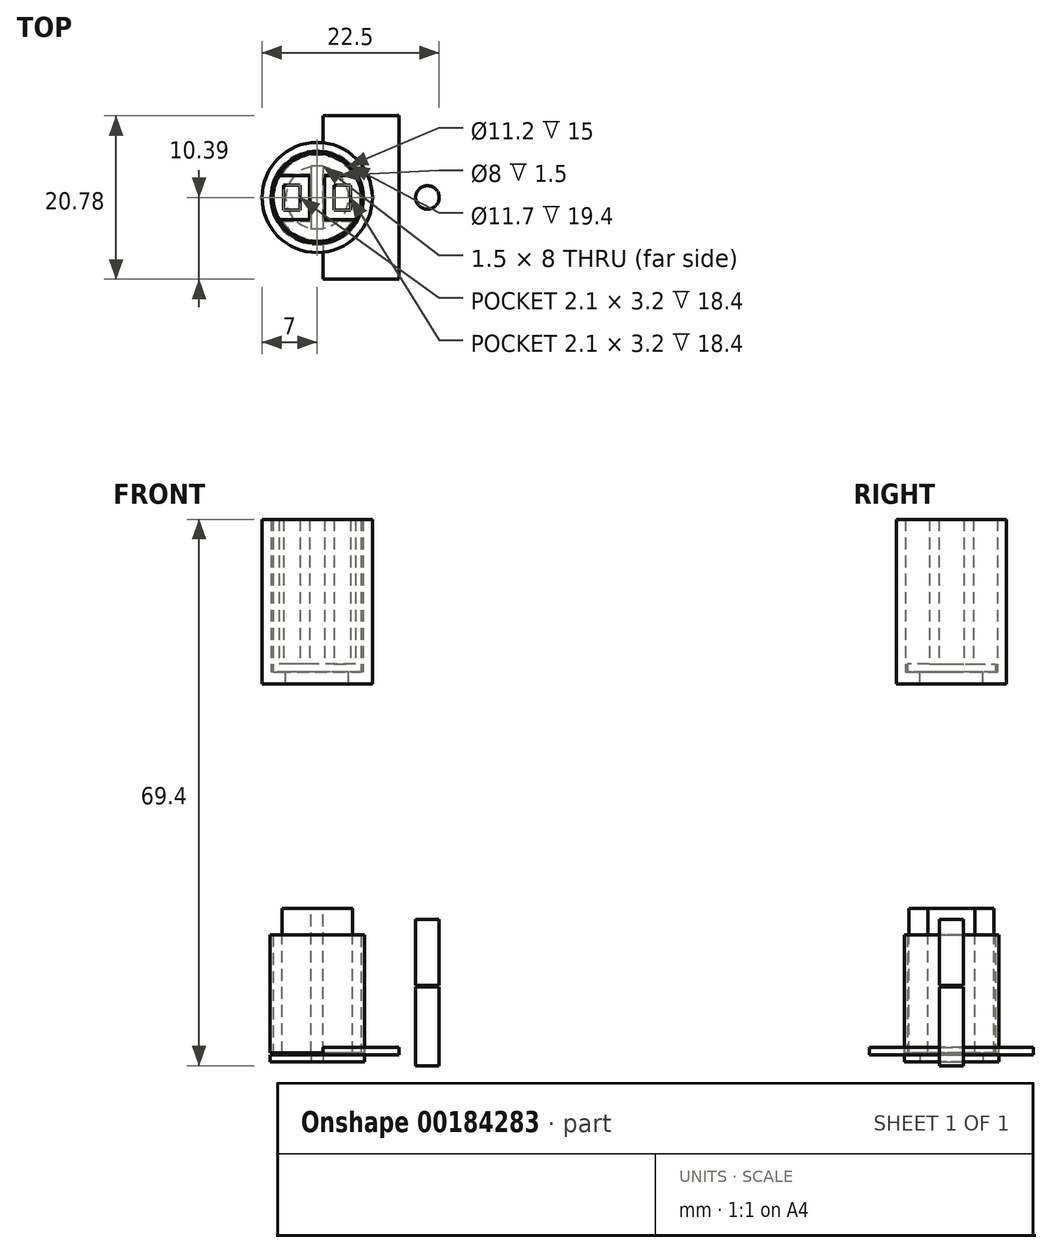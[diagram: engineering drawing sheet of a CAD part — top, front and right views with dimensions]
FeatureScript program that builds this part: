
annotation { "Feature Type Name" : "Feature", "Feature Type Description" : "" }
export const myFeature = defineFeature(function(context is Context, id is Id, definition is map)
    precondition{}
    {
        {
            assignVariable(context, id + "F0", {"name" : "dMaskThick", "anyValue" : .9});
        }
        {
            assignVariable(context, id + "F1", {"name" : "outerRingHeight", "anyValue" : 10});
        }
        {
            assignVariable(context, id + "F2", {"name" : "bottomLip", "anyValue" : .5});
        }
        {
            assignVariable(context, id + "F3", {"name" : "innerSquareHeight", "anyValue" : getVariable(context, 'outerRingHeight') - getVariable(context, 'dMaskThick') - getVariable(context, 'bottomLip')});
        }
        {
            assignVariable(context, id + "F4", {"name" : "innerRingHeight", "anyValue" : 15});
        }
        {
            var Q0;
            Q0=qCreatedBy(makeId("Top.planeOp"),FACE);
            var sketch = newSketch(context, id + "F5", { "sketchPlane" : qUnion([Q0])});
            skCircle(sketch, "E0", {"center": v(0, 0) * mm, "radius": 6 * mm});
            skCircle(sketch, "E1", {"center": v(0, 0) * mm, "radius": 17 * mm});
            skCircle(sketch, "E2", {"center": v(0, 0) * mm, "radius": 8.1 * mm});
            skCircle(sketch, "E3.cCircle", {"center": v(0, 0) * mm, "radius": 15 * mm});
            skLineSegment(sketch, "E3.0", {"start": v(10.6, -10.6) * mm, "end": v(-10.6, -10.6) * mm});
            skLineSegment(sketch, "E3.1", {"start": v(-10.6, -10.6) * mm, "end": v(-10.6, 10.6) * mm});
            skLineSegment(sketch, "E3.2", {"start": v(-10.6, 10.6) * mm, "end": v(10.6, 10.6) * mm});
            skLineSegment(sketch, "E3.3", {"start": v(10.6, 10.6) * mm, "end": v(10.6, -10.6) * mm});
            skLineSegment(sketch, "E4", {"start": v(-25.02, 0) * mm, "end": v(35.29, 0) * mm, "construction": true});
            skLineSegment(sketch, "E5", {"start": v(0, 24.03) * mm, "end": v(0, -20.76) * mm, "construction": true});
            skSolve(sketch);
        }
        {
            var Q0;
            Q0=makeQuery(id+"F5.imprint","IMPRINT",FACE,{"disambiguationData":[TD([[makeQuery(id+"F5.imprint","IMPRINT",EDGE,{"derivedFrom":sQuery(id+"F5.wireOp",EDGE,"E1")}),1.0]])]});
            var Q1;
            {var subQ0=sQuery(id+"F5.wireOp",EDGE,"E3.2");Q1=makeQuery(id+"F5.imprint","IMPRINT",FACE,{"disambiguationData":[TD([[makeQuery(id+"F5.imprint","IMPRINT",EDGE,{"derivedFrom":subQ0}),1.0]])]});}
            var Q2;
            {var subQ0=sQuery(id+"F5.wireOp",EDGE,"E3.1");Q2=makeQuery(id+"F5.imprint","IMPRINT",FACE,{"disambiguationData":[TD([[makeQuery(id+"F5.imprint","IMPRINT",EDGE,{"derivedFrom":subQ0}),1.0]])]});}
            var Q3;
            {var subQ0=sQuery(id+"F5.wireOp",EDGE,"E3.3");Q3=makeQuery(id+"F5.imprint","IMPRINT",FACE,{"disambiguationData":[TD([[makeQuery(id+"F5.imprint","IMPRINT",EDGE,{"derivedFrom":subQ0}),1.0]])]});}
            var Q4;
            {var subQ0=sQuery(id+"F5.wireOp",EDGE,"E3.0");Q4=makeQuery(id+"F5.imprint","IMPRINT",FACE,{"disambiguationData":[TD([[makeQuery(id+"F5.imprint","IMPRINT",EDGE,{"derivedFrom":subQ0}),1.0]])]});}
            var Q5;
            Q5=makeQuery(id+"F5.imprint","IMPRINT",FACE,{"disambiguationData":[TD([[makeQuery(id+"F5.imprint","IMPRINT",EDGE,{"derivedFrom":sQuery(id+"F5.wireOp",EDGE,"E2")}),-1.0]])]});
            var Q6;
            Q6=makeQuery(id+"F5.imprint","IMPRINT",FACE,{"disambiguationData":[TD([[makeQuery(id+"F5.imprint","IMPRINT",EDGE,{"derivedFrom":sQuery(id+"F5.wireOp",EDGE,"E0")}),-1.0]])]});
            extrude(context, id + "F6", {"entities" : qUnion([Q0, Q1, Q2, Q3, Q4, Q5, Q6]), "depth" : (getVariable(context, 'bottomLip')) * mm});
        }
        {
            var Q0;
            Q0=makeQuery(id+"F5.imprint","IMPRINT",FACE,{"disambiguationData":[TD([[makeQuery(id+"F5.imprint","IMPRINT",EDGE,{"derivedFrom":sQuery(id+"F5.wireOp",EDGE,"E1")}),1.0]])]});
            var Q1;
            {var subQ0=sQuery(id+"F5.wireOp",EDGE,"E3.1");Q1=makeQuery(id+"F5.imprint","IMPRINT",FACE,{"disambiguationData":[TD([[makeQuery(id+"F5.imprint","IMPRINT",EDGE,{"derivedFrom":subQ0}),1.0]])]});}
            var Q2;
            {var subQ0=sQuery(id+"F5.wireOp",EDGE,"E3.2");Q2=makeQuery(id+"F5.imprint","IMPRINT",FACE,{"disambiguationData":[TD([[makeQuery(id+"F5.imprint","IMPRINT",EDGE,{"derivedFrom":subQ0}),1.0]])]});}
            var Q3;
            {var subQ0=sQuery(id+"F5.wireOp",EDGE,"E3.3");Q3=makeQuery(id+"F5.imprint","IMPRINT",FACE,{"disambiguationData":[TD([[makeQuery(id+"F5.imprint","IMPRINT",EDGE,{"derivedFrom":subQ0}),1.0]])]});}
            var Q4;
            {var subQ0=sQuery(id+"F5.wireOp",EDGE,"E3.0");Q4=makeQuery(id+"F5.imprint","IMPRINT",FACE,{"disambiguationData":[TD([[makeQuery(id+"F5.imprint","IMPRINT",EDGE,{"derivedFrom":subQ0}),1.0]])]});}
            extrude(context, id + "F7", {"entities" : qUnion([Q0, Q1, Q2, Q3, Q4]), "operationType" : NewBodyOperationType.ADD, "depth" : getVariable(context, 'outerRingHeight') * mm});
        }
        {
            var Q0;
            Q0=makeQuery(id+"F6.opExtrude","CAP_FACE",FACE,{"disambiguationData":[OSD([sQuery(id+"F5.wireOp",EDGE,"E0"),sQuery(id+"F5.wireOp",EDGE,"E1")])],"isStart":false});
            var sketch = newSketch(context, id + "F8", { "sketchPlane" : qUnion([Q0])});
            skCircle(sketch, "E6.cCircle", {"center": v(0, 0) * mm, "radius": 14.7 * mm, "construction": true});
            skLineSegment(sketch, "E6.0", {"start": v(10.4, 10.4) * mm, "end": v(10.4, -10.4) * mm});
            skLineSegment(sketch, "E6.1", {"start": v(10.4, -10.4) * mm, "end": v(-10.4, -10.4) * mm});
            skLineSegment(sketch, "E6.2", {"start": v(-10.4, -10.4) * mm, "end": v(-10.4, 10.4) * mm});
            skLineSegment(sketch, "E6.3", {"start": v(-10.4, 10.4) * mm, "end": v(10.4, 10.4) * mm});
            skLineSegment(sketch, "E7.bottom", {"start": v(0.75, 4) * mm, "end": v(-0.75, 4) * mm});
            skLineSegment(sketch, "E7.top", {"start": v(0.75, -4) * mm, "end": v(-0.75, -4) * mm});
            skLineSegment(sketch, "E7.left", {"start": v(0.75, 4) * mm, "end": v(0.75, -4) * mm});
            skLineSegment(sketch, "E7.right", {"start": v(-0.75, 4) * mm, "end": v(-0.75, -4) * mm});
            skSolve(sketch);
        }
        {
            var Q0;
            Q0=makeQuery(id+"F8.imprint","IMPRINT",FACE,{"disambiguationData":[TD([[makeQuery(id+"F8.imprint","IMPRINT",EDGE,{"derivedFrom":sQuery(id+"F8.wireOp",EDGE,"E7.bottom")}),-1.0]])]});
            var Q1;
            Q1=makeQuery(id+"F8.imprint","IMPRINT",FACE,{"disambiguationData":[TD([[makeQuery(id+"F8.imprint","IMPRINT",EDGE,{"derivedFrom":sQuery(id+"F8.wireOp",EDGE,"E6.0")}),-1.0]])]});
            extrude(context, id + "F9", {"entities" : qUnion([Q0, Q1]), "depth" : (getVariable(context, 'dMaskThick')) * mm});
        }
        {
            var Q0;
            Q0=makeQuery(id+"F9.opExtrude","CAP_FACE",FACE,{"disambiguationData":[OSD([sQuery(id+"F8.wireOp",EDGE,"E6.0"),sQuery(id+"F8.wireOp",EDGE,"E6.1"),sQuery(id+"F8.wireOp",EDGE,"E6.2"),sQuery(id+"F8.wireOp",EDGE,"E6.3"),sQuery(id+"F8.wireOp",EDGE,"E7.bottom"),sQuery(id+"F8.wireOp",EDGE,"E7.top"),sQuery(id+"F8.wireOp",EDGE,"E7.left"),sQuery(id+"F8.wireOp",EDGE,"E7.right")])],"isStart":false});
            var sketch = newSketch(context, id + "F10", { "sketchPlane" : qUnion([Q0])});
            skCircle(sketch, "E8.cCircle", {"center": v(0, 0) * mm, "radius": 14.4 * mm, "construction": true});
            skLineSegment(sketch, "E8.0", {"start": v(10.18, 10.18) * mm, "end": v(10.18, -10.18) * mm});
            skLineSegment(sketch, "E8.1", {"start": v(10.18, -10.18) * mm, "end": v(-10.18, -10.18) * mm});
            skLineSegment(sketch, "E8.2", {"start": v(-10.18, -10.18) * mm, "end": v(-10.18, 10.18) * mm});
            skLineSegment(sketch, "E8.3", {"start": v(-10.18, 10.18) * mm, "end": v(10.18, 10.18) * mm});
            skCircle(sketch, "E9", {"center": v(0, 0) * mm, "radius": 8.1 * mm});
            skSolve(sketch);
        }
        {
            var Q0;
            Q0=qSketchRegion(id+"F10",true);
            extrude(context, id + "F11", {"entities" : qUnion([Q0]), "depth" : (getVariable(context, 'innerSquareHeight')) * mm});
        }
        {
            var Q0;
            Q0=qCreatedBy(makeId("Front.planeOp"),FACE);
            var sketch = newSketch(context, id + "F12", { "sketchPlane" : qUnion([Q0])});
            skCircle(sketch, "E10", {"center": v(8.5, 4) * mm, "radius": 1.1 * mm});
            skLineSegment(sketch, "E11", {"start": v(0, 23.51) * mm, "end": v(0, 0) * mm, "construction": true});
            skCircle(sketch, "E12", {"center": v(8.5, 7.44) * mm, "radius": 1.1 * mm});
            skCircle(sketch, "E13", {"center": v(8.5, 7.44) * mm, "radius": 1 * mm});
            skCircle(sketch, "E14", {"center": v(8.5, 4) * mm, "radius": 1 * mm});
            skSolve(sketch);
        }
        {
            var Q0;
            Q0=makeQuery(id+"F12.imprint","IMPRINT",FACE,{"disambiguationData":[TD([[makeQuery(id+"F12.imprint","IMPRINT",EDGE,{"derivedFrom":sQuery(id+"F12.wireOp",EDGE,"E13")}),1.0]])]});
            var Q1;
            Q1=makeQuery(id+"F12.imprint","IMPRINT",FACE,{"disambiguationData":[TD([[makeQuery(id+"F12.imprint","IMPRINT",EDGE,{"derivedFrom":sQuery(id+"F12.wireOp",EDGE,"E12")}),1.0]])]});
            var Q2;
            Q2=makeQuery(id+"F12.imprint","IMPRINT",FACE,{"disambiguationData":[TD([[makeQuery(id+"F12.imprint","IMPRINT",EDGE,{"derivedFrom":sQuery(id+"F12.wireOp",EDGE,"E14")}),1.0]])]});
            var Q3;
            Q3=makeQuery(id+"F12.imprint","IMPRINT",FACE,{"disambiguationData":[TD([[makeQuery(id+"F12.imprint","IMPRINT",EDGE,{"derivedFrom":sQuery(id+"F12.wireOp",EDGE,"E10")}),1.0]])]});
            var Q4;
            Q4=sQuery(id+"F12.wireOp",EDGE,"E11");
            revolve(context, id + "F13", {"operationType" : NewBodyOperationType.REMOVE, "entities" : qUnion([Q0, Q1, Q2, Q3]), "axis" : qUnion([Q4]), "revolveType" : RevolveType.FULL, "oppositeDirection" : true});
        }
        {
            var Q0;
            Q0=qCreatedBy(makeId("Front.planeOp"),FACE);
            var sketch = newSketch(context, id + "F14", { "sketchPlane" : qUnion([Q0])});
            skLineSegment(sketch, "E15", {"start": v(0, -4.37) * mm, "end": v(0, 15.91) * mm, "construction": true});
            skLineSegment(sketch, "E16", {"start": v(-23.99, 0) * mm, "end": v(22.47, 0) * mm, "construction": true});
            skLineSegment(sketch, "E17.bottom", {"start": v(5.6, 16.6) * mm, "end": v(7.6, 16.6) * mm});
            skLineSegment(sketch, "E17.top", {"start": v(5.6, 1.6) * mm, "end": v(7.6, 1.6) * mm});
            skLineSegment(sketch, "E17.left", {"start": v(5.6, 16.6) * mm, "end": v(5.6, 1.6) * mm});
            skLineSegment(sketch, "E17.right", {"start": v(7.6, 16.6) * mm, "end": v(7.6, 1.6) * mm});
            skSolve(sketch);
        }
        {
            var Q0;
            Q0=makeQuery(id+"F14.imprint","IMPRINT",FACE,{"disambiguationData":[TD([[makeQuery(id+"F14.imprint","IMPRINT",EDGE,{"derivedFrom":sQuery(id+"F14.wireOp",EDGE,"E17.bottom")}),-1.0]])]});
            var Q1;
            Q1=sQuery(id+"F14.wireOp",EDGE,"E15");
            revolve(context, id + "F15", {"entities" : qUnion([Q0]), "axis" : qUnion([Q1]), "revolveType" : RevolveType.FULL});
        }
        {
            var Q0;
            Q0=makeQuery(id+"F12.imprint","IMPRINT",FACE,{"disambiguationData":[TD([[makeQuery(id+"F12.imprint","IMPRINT",EDGE,{"derivedFrom":sQuery(id+"F12.wireOp",EDGE,"E13")}),1.0]])]});
            var Q1;
            Q1=makeQuery(id+"F12.imprint","IMPRINT",FACE,{"disambiguationData":[TD([[makeQuery(id+"F12.imprint","IMPRINT",EDGE,{"derivedFrom":sQuery(id+"F12.wireOp",EDGE,"E14")}),1.0]])]});
            var Q2;
            Q2=sQuery(id+"F12.wireOp",EDGE,"E11");
            revolve(context, id + "F16", {"entities" : qUnion([Q0, Q1]), "axis" : qUnion([Q2]), "revolveType" : RevolveType.FULL});
        }
        {
            var Q0;
            Q0=qCreatedBy(makeId("Top.planeOp"),FACE);
            cPlane(context, id + "F17", {"entities" : qUnion([Q0]), "cplaneType" : CPlaneType.OFFSET, "offset" : 16.6 * mm, "width" : 150 * mm, "height" : 150 * mm});
        }
        {
            var Q0;
            Q0=qCreatedBy(id+"F17.planeOp",FACE);
            var sketch = newSketch(context, id + "F18", { "sketchPlane" : qUnion([Q0])});
            skCircle(sketch, "E18", {"center": v(0, 0) * mm, "radius": 6 * mm});
            skCircle(sketch, "E19", {"center": v(0, 0) * mm, "radius": 17 * mm});
            skCircle(sketch, "E20", {"center": v(0, 0) * mm, "radius": 8.2 * mm});
            skCircle(sketch, "E21.cCircle", {"center": v(0, 0) * mm, "radius": 15 * mm});
            skLineSegment(sketch, "E21.0", {"start": v(10.6, -10.6) * mm, "end": v(-10.6, -10.6) * mm});
            skLineSegment(sketch, "E21.1", {"start": v(-10.6, -10.6) * mm, "end": v(-10.6, 10.6) * mm});
            skLineSegment(sketch, "E21.2", {"start": v(-10.6, 10.6) * mm, "end": v(10.6, 10.6) * mm});
            skLineSegment(sketch, "E21.3", {"start": v(10.6, 10.6) * mm, "end": v(10.6, -10.6) * mm});
            skLineSegment(sketch, "E22", {"start": v(0, 24.03) * mm, "end": v(0, -20.76) * mm, "construction": true});
            skSolve(sketch);
        }
        {
            var Q0;
            {var subQ0=sQuery(id+"F18.wireOp",EDGE,"E21.2");Q0=makeQuery(id+"F18.imprint","IMPRINT",FACE,{"disambiguationData":[TD([[makeQuery(id+"F18.imprint","IMPRINT",EDGE,{"derivedFrom":subQ0}),1.0]])]});}
            var Q1;
            Q1=makeQuery(id+"F18.imprint","IMPRINT",FACE,{"disambiguationData":[TD([[makeQuery(id+"F18.imprint","IMPRINT",EDGE,{"derivedFrom":sQuery(id+"F18.wireOp",EDGE,"E20")}),-1.0]])]});
            var Q2;
            {var subQ0=sQuery(id+"F18.wireOp",EDGE,"E21.1");Q2=makeQuery(id+"F18.imprint","IMPRINT",FACE,{"disambiguationData":[TD([[makeQuery(id+"F18.imprint","IMPRINT",EDGE,{"derivedFrom":subQ0}),1.0]])]});}
            var Q3;
            {var subQ0=sQuery(id+"F18.wireOp",EDGE,"E21.0");Q3=makeQuery(id+"F18.imprint","IMPRINT",FACE,{"disambiguationData":[TD([[makeQuery(id+"F18.imprint","IMPRINT",EDGE,{"derivedFrom":subQ0}),1.0]])]});}
            var Q4;
            {var subQ0=sQuery(id+"F18.wireOp",EDGE,"E21.3");Q4=makeQuery(id+"F18.imprint","IMPRINT",FACE,{"disambiguationData":[TD([[makeQuery(id+"F18.imprint","IMPRINT",EDGE,{"derivedFrom":subQ0}),1.0]])]});}
            var Q5;
            Q5=makeQuery(id+"F18.imprint","IMPRINT",FACE,{"disambiguationData":[TD([[makeQuery(id+"F18.imprint","IMPRINT",EDGE,{"derivedFrom":sQuery(id+"F18.wireOp",EDGE,"E19")}),1.0]])]});
            var Q6;
            Q6=makeQuery(id+"F18.imprint","IMPRINT",FACE,{"disambiguationData":[TD([[makeQuery(id+"F18.imprint","IMPRINT",EDGE,{"derivedFrom":sQuery(id+"F18.wireOp",EDGE,"E18")}),-1.0]])]});
            extrude(context, id + "F19", {"entities" : qUnion([Q0, Q1, Q2, Q3, Q4, Q5, Q6]), "depth" : 2 * mm});
        }
        {
            var Q0;
            Q0=makeQuery(id+"F18.imprint","IMPRINT",FACE,{"disambiguationData":[TD([[makeQuery(id+"F18.imprint","IMPRINT",EDGE,{"derivedFrom":sQuery(id+"F18.wireOp",EDGE,"E19")}),1.0]])]});
            var Q1;
            {var subQ0=sQuery(id+"F18.wireOp",EDGE,"E21.0");Q1=makeQuery(id+"F18.imprint","IMPRINT",FACE,{"disambiguationData":[TD([[makeQuery(id+"F18.imprint","IMPRINT",EDGE,{"derivedFrom":subQ0}),1.0]])]});}
            var Q2;
            {var subQ0=sQuery(id+"F18.wireOp",EDGE,"E21.1");Q2=makeQuery(id+"F18.imprint","IMPRINT",FACE,{"disambiguationData":[TD([[makeQuery(id+"F18.imprint","IMPRINT",EDGE,{"derivedFrom":subQ0}),1.0]])]});}
            var Q3;
            {var subQ0=sQuery(id+"F18.wireOp",EDGE,"E21.3");Q3=makeQuery(id+"F18.imprint","IMPRINT",FACE,{"disambiguationData":[TD([[makeQuery(id+"F18.imprint","IMPRINT",EDGE,{"derivedFrom":subQ0}),1.0]])]});}
            var Q4;
            {var subQ0=sQuery(id+"F18.wireOp",EDGE,"E21.2");Q4=makeQuery(id+"F18.imprint","IMPRINT",FACE,{"disambiguationData":[TD([[makeQuery(id+"F18.imprint","IMPRINT",EDGE,{"derivedFrom":subQ0}),1.0]])]});}
            extrude(context, id + "F20", {"entities" : qUnion([Q0, Q1, Q2, Q3, Q4]), "operationType" : NewBodyOperationType.ADD, "oppositeDirection" : true, "depth" : (getVariable(context, 'innerRingHeight') - getVariable(context, 'outerRingHeight') + getVariable(context, 'bottomLip') + getVariable(context, 'dMaskThick')) * mm});
        }
        {
            var Q0;
            Q0=makeQuery(id+"F19.opExtrude","CAP_FACE",FACE,{"disambiguationData":[OSD([sQuery(id+"F18.wireOp",EDGE,"E18"),sQuery(id+"F18.wireOp",EDGE,"E19")])],"isStart":false});
            var sketch = newSketch(context, id + "F21", { "sketchPlane" : qUnion([Q0])});
            skCircle(sketch, "E23", {"center": v(-14, 0) * mm, "radius": 1.5 * mm});
            skLineSegment(sketch, "E24", {"start": v(0, 21.2) * mm, "end": v(0, -23.2) * mm, "construction": true});
            skCircle(sketch, "E25.MirrorC", {"center": v(14, 0) * mm, "radius": 1.5 * mm});
            skSolve(sketch);
        }
        {
            var Q0;
            Q0=makeQuery(id+"F21.imprint","IMPRINT",FACE,{"disambiguationData":[TD([[makeQuery(id+"F21.imprint","IMPRINT",EDGE,{"derivedFrom":sQuery(id+"F21.wireOp",EDGE,"E23")}),1.0]])]});
            var Q1;
            Q1=makeQuery(id+"F21.imprint","IMPRINT",FACE,{"disambiguationData":[TD([[makeQuery(id+"F21.imprint","IMPRINT",EDGE,{"derivedFrom":sQuery(id+"F21.wireOp",EDGE,"E25.MirrorC")}),-1.0]])]});
            var Q2;
            Q2=makeQuery(id+"F6.opExtrude","CAP_FACE",FACE,{"disambiguationData":[OSD([sQuery(id+"F5.wireOp",EDGE,"E0"),sQuery(id+"F5.wireOp",EDGE,"E1")])],"isStart":true});
            extrude(context, id + "F22", {"entities" : qUnion([Q0, Q1]), "operationType" : NewBodyOperationType.REMOVE, "endBound" : BoundingType.UP_TO_SURFACE, "oppositeDirection" : true, "endBoundEntityFace" : qUnion([Q2]), "depth" : 25 * mm});
        }
        {
            var Q0;
            Q0=qCreatedBy(makeId("Top.planeOp"),FACE);
            cPlane(context, id + "F23", {"entities" : qUnion([Q0]), "cplaneType" : CPlaneType.OFFSET, "offset" : 20 * mm, "width" : 150 * mm, "height" : 150 * mm});
        }
        {
            var Q0;
            Q0=qCreatedBy(id+"F23.planeOp",FACE);
            var sketch = newSketch(context, id + "F24", { "sketchPlane" : qUnion([Q0])});
            skArc(sketch, "E26", {"start": v(-4.49, -3) * mm, "mid": v(0, -5.4) * mm, "end": v(4.49, -3) * mm});
            skLineSegment(sketch, "E27", {"start": v(0, 5.4) * mm, "end": v(0, -5.4) * mm, "construction": true});
            skLineSegment(sketch, "E28", {"start": v(5.4, 0) * mm, "end": v(-5.4, 0) * mm, "construction": true});
            skLineSegment(sketch, "E29", {"start": v(-4.49, 3) * mm, "end": v(-0.75, 3) * mm});
            skLineSegment(sketch, "E30", {"start": v(-0.75, 3) * mm, "end": v(-0.75, 0) * mm});
            skLineSegment(sketch, "E31", {"start": v(0.75, 3) * mm, "end": v(0.75, 0) * mm});
            skLineSegment(sketch, "E32.MirrorCS", {"start": v(0.75, -3) * mm, "end": v(0.75, 0) * mm});
            skLineSegment(sketch, "E33.MirrorCS", {"start": v(-0.75, -3) * mm, "end": v(-0.75, 0) * mm});
            skLineSegment(sketch, "E34.MirrorCS", {"start": v(-4.49, -3) * mm, "end": v(-0.75, -3) * mm});
            skLineSegment(sketch, "E35.trimOffspring", {"start": v(0.75, -3) * mm, "end": v(4.49, -3) * mm});
            skLineSegment(sketch, "E36.trimOffspring", {"start": v(0.75, 3) * mm, "end": v(4.49, 3) * mm});
            skArc(sketch, "E37.trimOffspring", {"start": v(4.49, 3) * mm, "mid": v(0, 5.4) * mm, "end": v(-4.49, 3) * mm});
            skSolve(sketch);
        }
        {
            var Q0;
            Q0 = qSketchRegion(id + "F24", true);
            var Q1;
            Q1=makeQuery(id+"F15.opRevolve","SWEPT_FACE",FACE,{"disambiguationData":[OSD([sQuery(id+"F14.wireOp",EDGE,"E17.top")])]});
            extrude(context, id + "F25", {"entities" : qUnion([Q0]), "endBound" : BoundingType.UP_TO_SURFACE, "oppositeDirection" : true, "endBoundEntityFace" : qUnion([Q1]), "depth" : 25 * mm});
        }
        {
            var Q0;
            Q0=qCreatedBy(id+"F23.planeOp",FACE);
            cPlane(context, id + "F26", {"entities" : qUnion([Q0]), "cplaneType" : CPlaneType.OFFSET, "offset" : 30 * mm, "width" : 150 * mm, "height" : 150 * mm});
        }
        {
            var Q0;
            Q0=qCreatedBy(id+"F26.planeOp",FACE);
            var sketch = newSketch(context, id + "F27", { "sketchPlane" : qUnion([Q0])});
            skCircle(sketch, "E38", {"center": v(0, 0) * mm, "radius": 5.6 * mm});
            skLineSegment(sketch, "E39", {"start": v(0, 5.6) * mm, "end": v(0, -5.6) * mm, "construction": true});
            skLineSegment(sketch, "E40", {"start": v(5.6, 0) * mm, "end": v(-5.6, 0) * mm, "construction": true});
            skLineSegment(sketch, "E41", {"start": v(-4.85, 2.8) * mm, "end": v(-0.95, 2.8) * mm});
            skLineSegment(sketch, "E42", {"start": v(-4.85, -2.8) * mm, "end": v(-0.95, -2.8) * mm});
            skLineSegment(sketch, "E43", {"start": v(-0.95, 2.8) * mm, "end": v(-0.95, -2.8) * mm});
            skLineSegment(sketch, "E44", {"start": v(0.95, -2.8) * mm, "end": v(0.95, 2.8) * mm});
            skLineSegment(sketch, "E45.trimOffspring", {"start": v(0.95, 2.8) * mm, "end": v(4.85, 2.8) * mm});
            skLineSegment(sketch, "E46.trimOffspring", {"start": v(0.95, -2.8) * mm, "end": v(4.85, -2.8) * mm});
            skLineSegment(sketch, "E47.bottom", {"start": v(4.25, 1.6) * mm, "end": v(2.15, 1.6) * mm});
            skLineSegment(sketch, "E47.top", {"start": v(4.25, -1.6) * mm, "end": v(2.15, -1.6) * mm});
            skLineSegment(sketch, "E47.left", {"start": v(4.25, 1.6) * mm, "end": v(4.25, -1.6) * mm});
            skLineSegment(sketch, "E47.right", {"start": v(2.15, 1.6) * mm, "end": v(2.15, -1.6) * mm});
            skPoint(sketch, "E47.middle", {"position": v(3.2, 0) * mm});
            skPoint(sketch, "E48.MirrorP", {"position": v(-3.2, 0) * mm});
            skLineSegment(sketch, "E49.MirrorCS", {"start": v(-4.25, -1.6) * mm, "end": v(-2.15, -1.6) * mm});
            skLineSegment(sketch, "E50.MirrorCS", {"start": v(-2.15, 1.6) * mm, "end": v(-2.15, -1.6) * mm});
            skLineSegment(sketch, "E51.MirrorCS", {"start": v(-4.25, 1.6) * mm, "end": v(-4.25, -1.6) * mm});
            skLineSegment(sketch, "E52.MirrorCS", {"start": v(-4.25, 1.6) * mm, "end": v(-2.15, 1.6) * mm});
            skSolve(sketch);
        }
        {
            var Q0;
            Q0=makeQuery(id+"F27.imprint","IMPRINT",FACE,{"disambiguationData":[TD([[makeQuery(id+"F27.imprint","IMPRINT",EDGE,{"derivedFrom":sQuery(id+"F27.wireOp",EDGE,"E47.bottom")}),1.0]])]});
            var Q1;
            Q1=makeQuery(id+"F27.imprint","IMPRINT",FACE,{"disambiguationData":[TD([[makeQuery(id+"F27.imprint","IMPRINT",EDGE,{"derivedFrom":sQuery(id+"F27.wireOp",EDGE,"E44")}),-1.0]])]});
            var Q2;
            {var subQ0=sQuery(id+"F27.wireOp",EDGE,"E41");Q2=makeQuery(id+"F27.imprint","IMPRINT",FACE,{"disambiguationData":[TD([[makeQuery(id+"F27.imprint","IMPRINT",EDGE,{"derivedFrom":subQ0}),1.0]])]});}
            var Q3;
            {var subQ1=sQuery(id+"F27.wireOp",EDGE,"E41");Q3=makeQuery(id+"F27.imprint","IMPRINT",FACE,{"disambiguationData":[TD([[makeQuery(id+"F27.imprint","IMPRINT",EDGE,{"derivedFrom":subQ1}),-1.0]])]});}
            var Q4;
            Q4=makeQuery(id+"F27.imprint","IMPRINT",FACE,{"disambiguationData":[TD([[makeQuery(id+"F27.imprint","IMPRINT",EDGE,{"derivedFrom":sQuery(id+"F27.wireOp",EDGE,"E49.MirrorCS")}),1.0]])]});
            extrude(context, id + "F28", {"entities" : qUnion([Q0, Q1, Q2, Q3, Q4]), "depth" : 1 * mm});
        }
        {
            var Q0;
            {var subQ0=sQuery(id+"F27.wireOp",EDGE,"E41");Q0=makeQuery(id+"F27.imprint","IMPRINT",FACE,{"disambiguationData":[TD([[makeQuery(id+"F27.imprint","IMPRINT",EDGE,{"derivedFrom":subQ0}),-1.0]])]});}
            var Q1;
            Q1=makeQuery(id+"F27.imprint","IMPRINT",FACE,{"disambiguationData":[TD([[makeQuery(id+"F27.imprint","IMPRINT",EDGE,{"derivedFrom":sQuery(id+"F27.wireOp",EDGE,"E44")}),-1.0]])]});
            extrude(context, id + "F29", {"entities" : qUnion([Q0, Q1]), "operationType" : NewBodyOperationType.ADD, "depth" : 19.4 * mm});
        }
        {
            var Q0;
            Q0=qCreatedBy(id+"F26.planeOp",FACE);
            var sketch = newSketch(context, id + "F30", { "sketchPlane" : qUnion([Q0])});
            skCircle(sketch, "E53", {"center": v(0, 0) * mm, "radius": 7 * mm});
            skCircle(sketch, "E54", {"center": v(0, 0) * mm, "radius": 4 * mm});
            skCircle(sketch, "E55", {"center": v(0, 0) * mm, "radius": 5.85 * mm});
            skSolve(sketch);
        }
        {
            var Q0;
            Q0=makeQuery(id+"F30.imprint","IMPRINT",FACE,{"disambiguationData":[TD([[makeQuery(id+"F30.imprint","IMPRINT",EDGE,{"derivedFrom":sQuery(id+"F30.wireOp",EDGE,"E54")}),-1.0]])]});
            var Q1;
            Q1=makeQuery(id+"F30.imprint","IMPRINT",FACE,{"disambiguationData":[TD([[makeQuery(id+"F30.imprint","IMPRINT",EDGE,{"derivedFrom":sQuery(id+"F30.wireOp",EDGE,"E53")}),1.0]])]});
            extrude(context, id + "F31", {"entities" : qUnion([Q0, Q1]), "oppositeDirection" : true, "depth" : 1.5 * mm});
        }
        {
            var Q0;
            Q0=makeQuery(id+"F30.imprint","IMPRINT",FACE,{"disambiguationData":[TD([[makeQuery(id+"F30.imprint","IMPRINT",EDGE,{"derivedFrom":sQuery(id+"F30.wireOp",EDGE,"E53")}),1.0]])]});
            extrude(context, id + "F32", {"entities" : qUnion([Q0]), "operationType" : NewBodyOperationType.ADD, "depth" : 19.4 * mm});
        }
        {
            var Q0;
            Q0=makeQuery(id+"F9.opExtrude","CAP_FACE",FACE,{"disambiguationData":[OSD([sQuery(id+"F8.wireOp",EDGE,"E6.0"),sQuery(id+"F8.wireOp",EDGE,"E6.1"),sQuery(id+"F8.wireOp",EDGE,"E6.2"),sQuery(id+"F8.wireOp",EDGE,"E6.3"),sQuery(id+"F8.wireOp",EDGE,"E7.bottom"),sQuery(id+"F8.wireOp",EDGE,"E7.top"),sQuery(id+"F8.wireOp",EDGE,"E7.left"),sQuery(id+"F8.wireOp",EDGE,"E7.right")])],"isStart":false});
            var sketch = newSketch(context, id + "F33", { "sketchPlane" : qUnion([Q0])});
            skLineSegment(sketch, "E56.bottom", {"start": v(-0.75, 10.4) * mm, "end": v(-10.4, 10.4) * mm});
            skLineSegment(sketch, "E56.top", {"start": v(-0.75, -10.4) * mm, "end": v(-10.4, -10.4) * mm});
            skLineSegment(sketch, "E56.left", {"start": v(-0.75, 10.4) * mm, "end": v(-0.75, -10.4) * mm});
            skLineSegment(sketch, "E56.right", {"start": v(-10.4, 10.4) * mm, "end": v(-10.4, -10.4) * mm});
            skLineSegment(sketch, "E57.bottom", {"start": v(0.75, 10.4) * mm, "end": v(10.4, 10.4) * mm});
            skLineSegment(sketch, "E57.top", {"start": v(0.75, -10.4) * mm, "end": v(10.4, -10.4) * mm});
            skLineSegment(sketch, "E57.left", {"start": v(0.75, 10.4) * mm, "end": v(0.75, -10.4) * mm});
            skLineSegment(sketch, "E57.right", {"start": v(10.4, 10.4) * mm, "end": v(10.4, -10.4) * mm});
            skSolve(sketch);
        }
        {
            var Q0;
            {var subQ3=sQuery(id+"F33.wireOp",EDGE,"E56.bottom");Q0=makeQuery(id+"F33.imprint","IMPRINT",FACE,{"disambiguationData":[TD([[makeQuery(id+"F33.imprint","IMPRINT",EDGE,{"derivedFrom":subQ3}),-1.0]])]});}
            var Q1;
            {var subQ3=sQuery(id+"F33.wireOp",EDGE,"E57.bottom");Q1=makeQuery(id+"F33.imprint","IMPRINT",FACE,{"disambiguationData":[TD([[makeQuery(id+"F33.imprint","IMPRINT",EDGE,{"derivedFrom":subQ3}),-1.0]])]});}
            extrude(context, id + "F34", {"entities" : qUnion([Q0, Q1]), "depth" : (getVariable(context, 'dMaskThick')) * mm});
        }
    });
